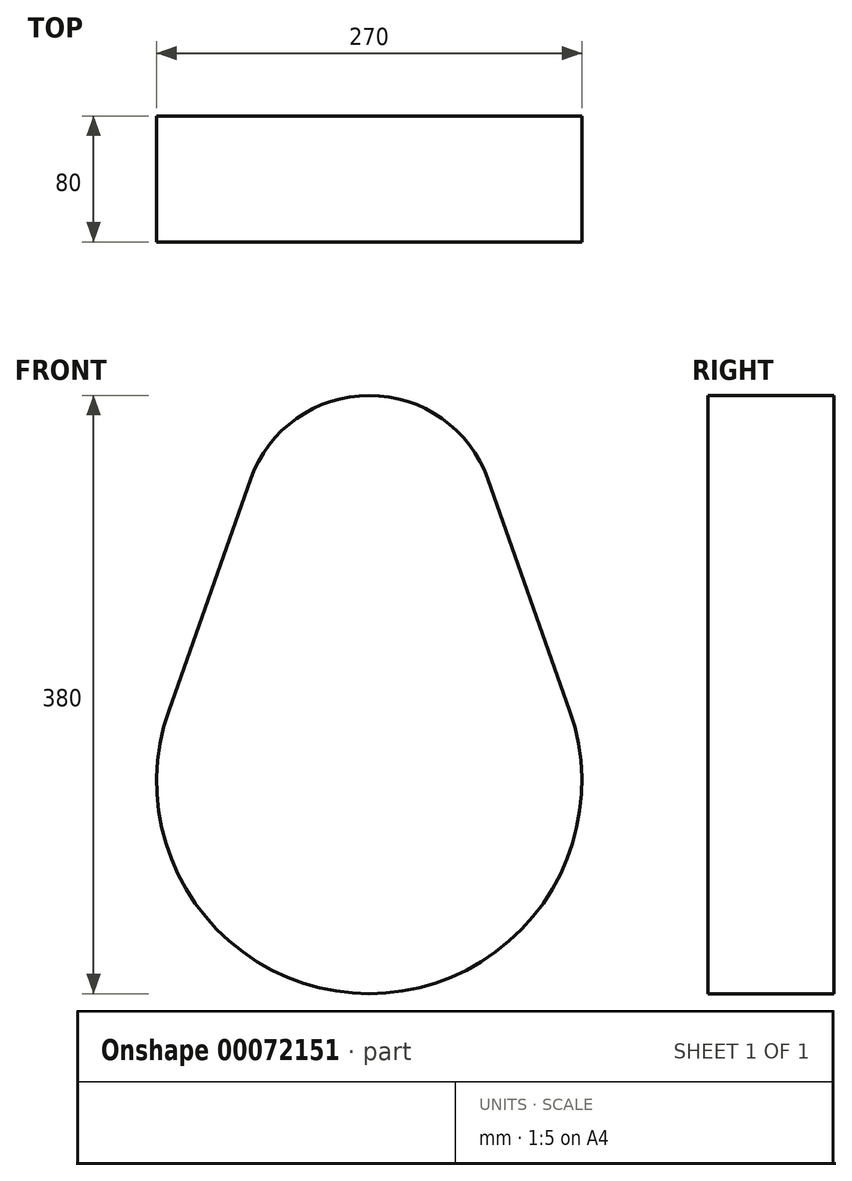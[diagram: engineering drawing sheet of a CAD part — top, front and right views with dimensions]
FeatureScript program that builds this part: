
annotation { "Feature Type Name" : "Feature", "Feature Type Description" : "" }
export const myFeature = defineFeature(function(context is Context, id is Id, definition is map)
    precondition{}
    {
        {
            var Q0;
            Q0=qCreatedBy(makeId("Front.planeOp"),FACE);
            var sketch = newSketch(context, id + "F0", { "sketchPlane" : qUnion([Q0])});
            skArc(sketch, "E0", {"start": v(-127.28, -146.67) * mm, "mid": v(0, -326.67) * mm, "end": v(127.28, -146.67) * mm});
            skArc(sketch, "E1", {"start": v(75.42, 0) * mm, "mid": v(0, 53.33) * mm, "end": v(-75.42, 0) * mm});
            skLineSegment(sketch, "E2", {"start": v(-75.42, 0) * mm, "end": v(-127.28, -146.67) * mm});
            skLineSegment(sketch, "E3", {"start": v(75.42, 0) * mm, "end": v(127.28, -146.67) * mm});
            skSolve(sketch);
        }
        {
            var Q0;
            Q0=makeQuery(id+"F0.imprint","IMPRINT",FACE,{"disambiguationData":[TD([[makeQuery(id+"F0.imprint","IMPRINT",EDGE,{"derivedFrom":sQuery(id+"F0.wireOp",EDGE,"E0")}),1.0]])]});
            extrude(context, id + "F1", {"entities" : qUnion([Q0]), "depth" : 80 * mm});
        }
    });
